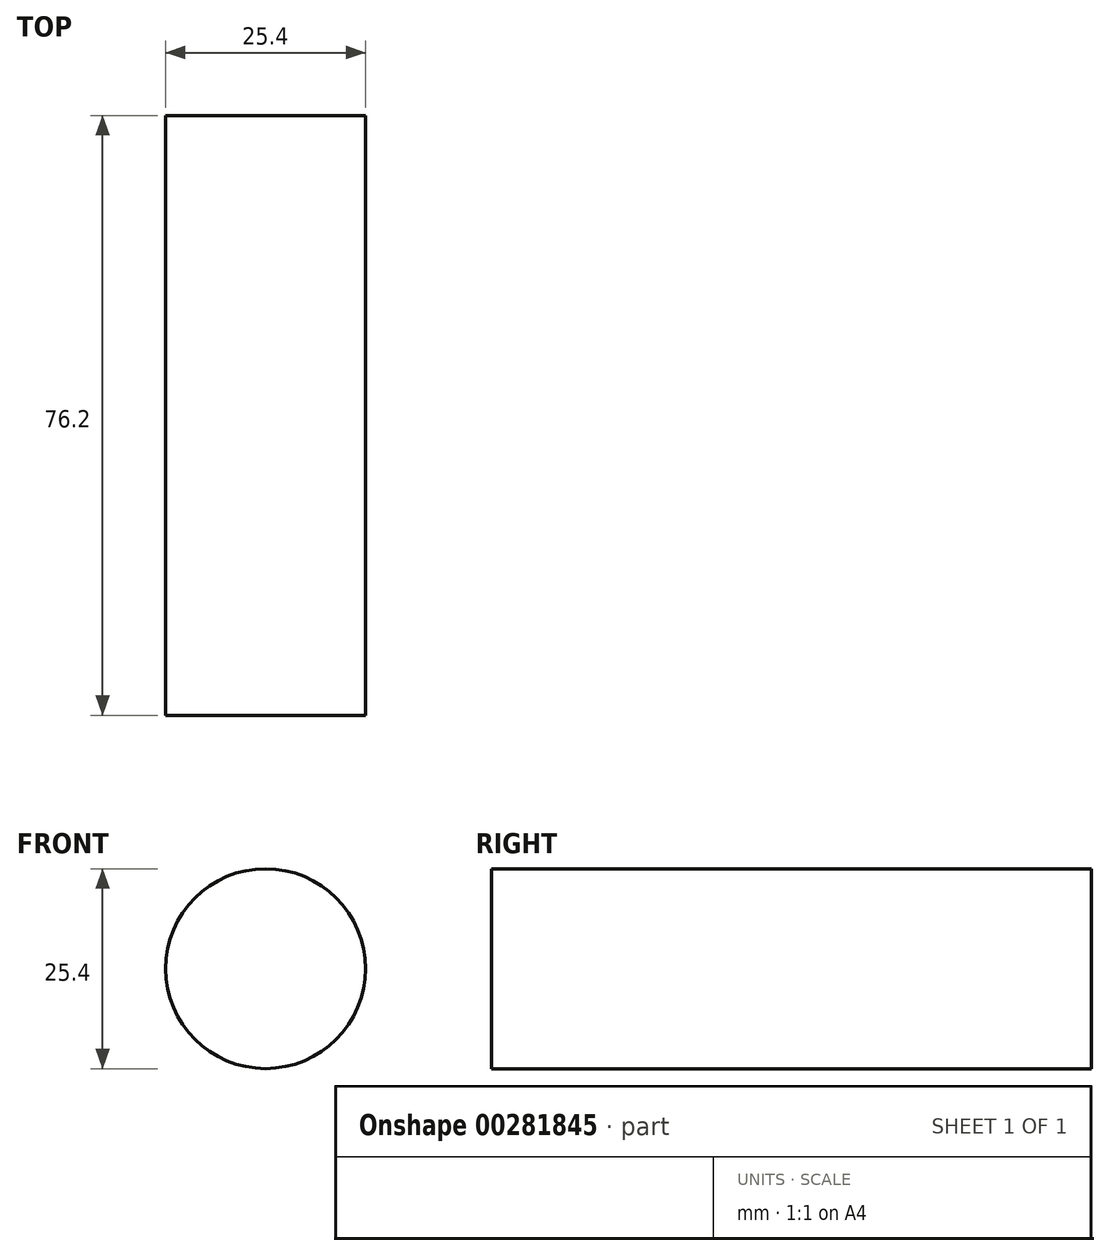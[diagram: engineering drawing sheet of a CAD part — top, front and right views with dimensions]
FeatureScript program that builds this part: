
annotation { "Feature Type Name" : "Feature", "Feature Type Description" : "" }
export const myFeature = defineFeature(function(context is Context, id is Id, definition is map)
    precondition{}
    {
        {
            var Q0;
            Q0=qCreatedBy(makeId("Front.planeOp"),FACE);
            var sketch = newSketch(context, id + "F0", { "sketchPlane" : qUnion([Q0])});
            skCircle(sketch, "E0", {"center": v(-27.88, 17) * mm, "radius": 12.7 * mm});
            skSolve(sketch);
        }
        {
            var Q0;
            Q0 = qSketchRegion(id + "F0", true);
            extrude(context, id + "F1", {"entities" : qUnion([Q0]), "depth" : 76.2 * mm});
        }
    });
